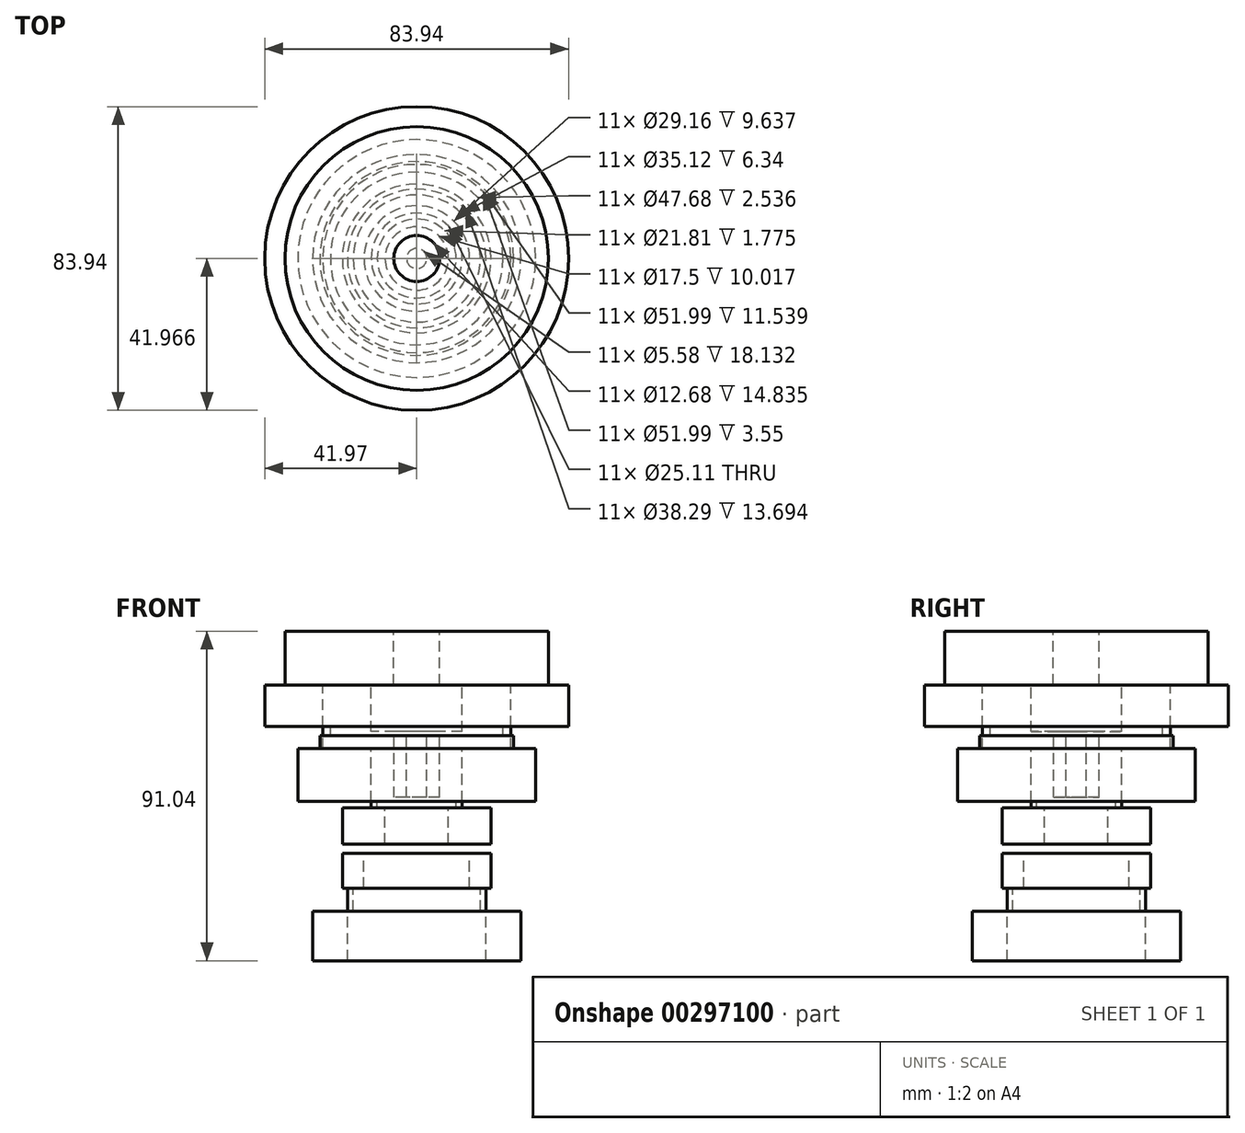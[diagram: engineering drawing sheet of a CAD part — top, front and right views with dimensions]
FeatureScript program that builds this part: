
annotation { "Feature Type Name" : "Feature", "Feature Type Description" : "" }
export const myFeature = defineFeature(function(context is Context, id is Id, definition is map)
    precondition{}
    {
        {
            var Q0;
            Q0=qCreatedBy(makeId("Right.planeOp"),FACE);
            var sketch = newSketch(context, id + "F0", { "sketchPlane" : qUnion([Q0])});
            skLineSegment(sketch, "E0.bottom", {"start": v(-18.39, 0) * mm, "end": v(-24.35, 0) * mm});
            skLineSegment(sketch, "E0.top", {"start": v(-18.39, 9.64) * mm, "end": v(-24.35, 9.64) * mm});
            skLineSegment(sketch, "E0.left", {"start": v(-18.39, 0) * mm, "end": v(-18.39, 9.64) * mm});
            skLineSegment(sketch, "E0.right", {"start": v(-24.35, 0) * mm, "end": v(-24.35, 9.64) * mm});
            skLineSegment(sketch, "E1.bottom", {"start": v(-24.35, 9.64) * mm, "end": v(-24.35, 9.64) * mm});
            skLineSegment(sketch, "E1.top", {"start": v(-24.35, 12.17) * mm, "end": v(-24.35, 12.17) * mm});
            skLineSegment(sketch, "E1.left", {"start": v(-24.35, 9.64) * mm, "end": v(-24.35, 12.17) * mm});
            skLineSegment(sketch, "E1.right", {"start": v(-24.35, 9.64) * mm, "end": v(-24.35, 12.17) * mm});
            skLineSegment(sketch, "E2.bottom", {"start": v(-24.35, 12.17) * mm, "end": v(-12.55, 12.17) * mm});
            skLineSegment(sketch, "E2.top", {"start": v(-24.35, 22.19) * mm, "end": v(-12.55, 22.19) * mm});
            skLineSegment(sketch, "E2.left", {"start": v(-24.35, 12.17) * mm, "end": v(-24.35, 22.19) * mm});
            skLineSegment(sketch, "E2.right", {"start": v(-12.55, 12.17) * mm, "end": v(-12.55, 22.19) * mm});
            skLineSegment(sketch, "E3.bottom", {"start": v(-14.7, 22.19) * mm, "end": v(-16.36, 22.19) * mm});
            skLineSegment(sketch, "E3.top", {"start": v(-14.7, 23.96) * mm, "end": v(-16.36, 23.96) * mm});
            skLineSegment(sketch, "E3.left", {"start": v(-14.7, 22.19) * mm, "end": v(-14.7, 23.96) * mm});
            skLineSegment(sketch, "E3.right", {"start": v(-16.36, 22.19) * mm, "end": v(-16.36, 23.96) * mm});
            skLineSegment(sketch, "E4.bottom", {"start": v(-16.36, 23.96) * mm, "end": v(-36.64, 23.96) * mm});
            skLineSegment(sketch, "E4.top", {"start": v(-16.36, 38.55) * mm, "end": v(-36.64, 38.55) * mm});
            skLineSegment(sketch, "E4.left", {"start": v(-16.36, 23.96) * mm, "end": v(-16.36, 38.55) * mm});
            skLineSegment(sketch, "E4.right", {"start": v(-36.64, 23.96) * mm, "end": v(-36.64, 38.55) * mm});
            skLineSegment(sketch, "E5.bottom", {"start": v(-30.56, 38.55) * mm, "end": v(-29.8, 38.55) * mm});
            skLineSegment(sketch, "E5.top", {"start": v(-30.56, 42.1) * mm, "end": v(-29.8, 42.1) * mm});
            skLineSegment(sketch, "E5.left", {"start": v(-30.56, 38.55) * mm, "end": v(-30.56, 42.1) * mm});
            skLineSegment(sketch, "E5.right", {"start": v(-29.8, 38.55) * mm, "end": v(-29.8, 42.1) * mm});
            skLineSegment(sketch, "E6.bottom", {"start": v(-29.8, 42.1) * mm, "end": v(-27.64, 42.1) * mm});
            skLineSegment(sketch, "E6.top", {"start": v(-29.8, 44.63) * mm, "end": v(-27.64, 44.63) * mm});
            skLineSegment(sketch, "E6.left", {"start": v(-29.8, 42.1) * mm, "end": v(-29.8, 44.63) * mm});
            skLineSegment(sketch, "E6.right", {"start": v(-27.64, 42.1) * mm, "end": v(-27.64, 44.63) * mm});
            skLineSegment(sketch, "E7.bottom", {"start": v(-29.8, 44.63) * mm, "end": v(-45.77, 44.63) * mm});
            skLineSegment(sketch, "E7.top", {"start": v(-29.8, 56.17) * mm, "end": v(-45.77, 56.17) * mm});
            skLineSegment(sketch, "E7.left", {"start": v(-29.8, 44.63) * mm, "end": v(-29.8, 56.17) * mm});
            skLineSegment(sketch, "E7.right", {"start": v(-45.77, 44.63) * mm, "end": v(-45.77, 56.17) * mm});
            skLineSegment(sketch, "E8.bottom", {"start": v(-40.2, 56.17) * mm, "end": v(-10.14, 56.17) * mm});
            skLineSegment(sketch, "E8.top", {"start": v(-40.2, 71) * mm, "end": v(-10.14, 71) * mm});
            skLineSegment(sketch, "E8.left", {"start": v(-40.2, 56.17) * mm, "end": v(-40.2, 71) * mm});
            skLineSegment(sketch, "E8.right", {"start": v(-10.14, 56.17) * mm, "end": v(-10.14, 71) * mm});
            skLineSegment(sketch, "E9.bottom", {"start": v(-16.36, 56.17) * mm, "end": v(-3.8, 56.17) * mm});
            skLineSegment(sketch, "E9.top", {"start": v(-16.36, 43.24) * mm, "end": v(-3.8, 43.24) * mm});
            skLineSegment(sketch, "E9.left", {"start": v(-16.36, 56.17) * mm, "end": v(-16.36, 43.24) * mm});
            skLineSegment(sketch, "E9.right", {"start": v(-3.8, 56.17) * mm, "end": v(-3.8, 43.24) * mm});
            skLineSegment(sketch, "E10.bottom", {"start": v(-10.08, 43.24) * mm, "end": v(-6.6, 43.24) * mm});
            skLineSegment(sketch, "E10.top", {"start": v(-10.08, 25.1) * mm, "end": v(-6.6, 25.1) * mm});
            skLineSegment(sketch, "E10.left", {"start": v(-10.08, 43.24) * mm, "end": v(-10.08, 25.1) * mm});
            skLineSegment(sketch, "E10.right", {"start": v(-6.6, 43.24) * mm, "end": v(-6.6, 25.1) * mm});
            skLineSegment(sketch, "E11.bottom", {"start": v(-21.37, 0) * mm, "end": v(-22.95, 0) * mm});
            skLineSegment(sketch, "E11.top", {"start": v(-21.37, -6.34) * mm, "end": v(-22.95, -6.34) * mm});
            skLineSegment(sketch, "E11.left", {"start": v(-21.37, 0) * mm, "end": v(-21.37, -6.34) * mm});
            skLineSegment(sketch, "E11.right", {"start": v(-22.95, 0) * mm, "end": v(-22.95, -6.34) * mm});
            skLineSegment(sketch, "E12.bottom", {"start": v(-22.95, -6.34) * mm, "end": v(-32.59, -6.34) * mm});
            skLineSegment(sketch, "E12.top", {"start": v(-22.95, -20.03) * mm, "end": v(-32.59, -20.03) * mm});
            skLineSegment(sketch, "E12.left", {"start": v(-22.95, -6.34) * mm, "end": v(-22.95, -20.03) * mm});
            skLineSegment(sketch, "E12.right", {"start": v(-32.59, -6.34) * mm, "end": v(-32.59, -20.03) * mm});
            skSolve(sketch);
        }
        {
            var Q0;
            Q0 = qSketchRegion(id + "F0", true);
            var Q1;
            Q1=sQuery(id+"F0.wireOp",EDGE,"E9.right");
            revolve(context, id + "F1", {"entities" : qUnion([Q0]), "axis" : qUnion([Q1]), "revolveType" : RevolveType.FULL});
        }
    });
